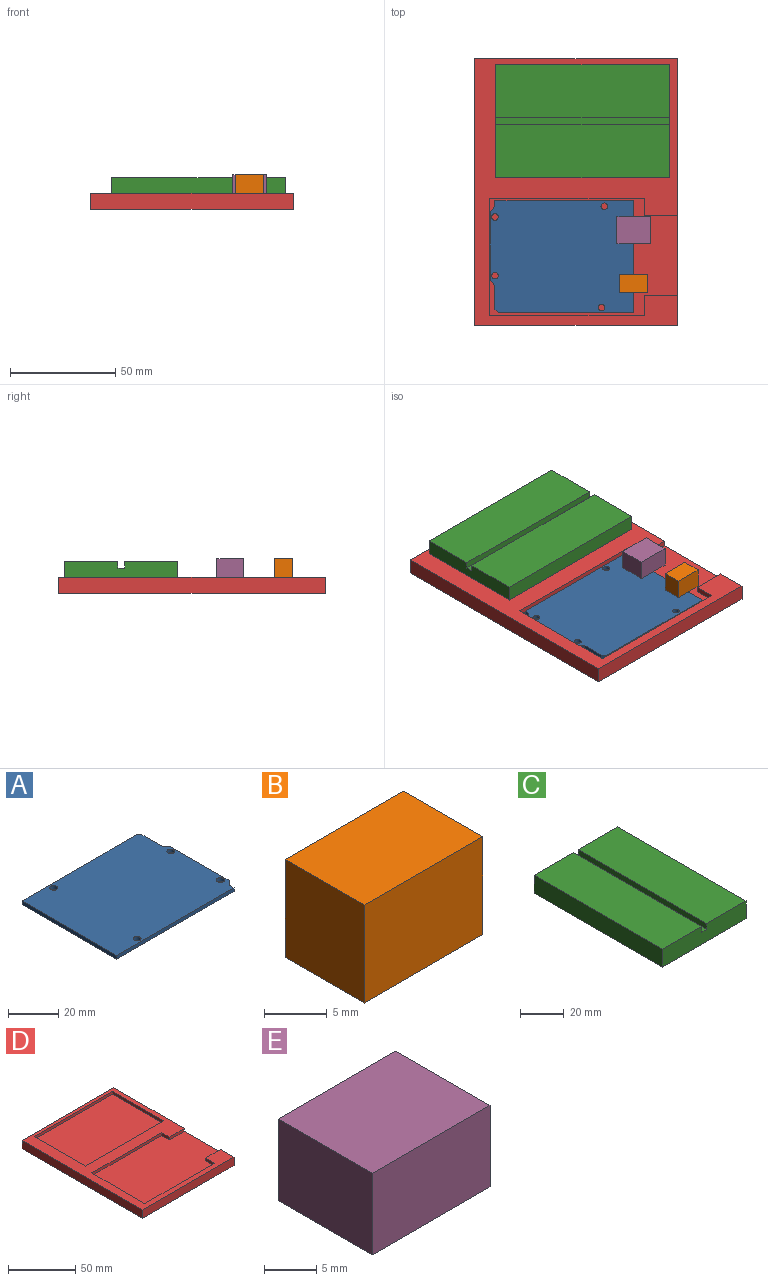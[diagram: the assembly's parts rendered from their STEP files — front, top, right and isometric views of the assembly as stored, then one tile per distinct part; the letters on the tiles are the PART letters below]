
ASSEMBLY  parts=5 mates=4
PART A: 15 faces, bbox 68.3x53.3x1.8 mm
  f0: plane 66.04x1.78mm, normal (0,-1,0), area 117.4mm2, adj f1,f11,f13,f14
  f1: plane 2.54x1.78mm, normal (1,0,0), area 4.5mm2, adj f0,f2,f13,f14
  f2: plane 2.54x2.27mm, normal (0.75,-0.67,0), area 6.1mm2, adj f1,f3,f13,f14
  f3: plane 32.77x1.78mm, normal (1,0,0), area 58.3mm2, adj f2,f4,f13,f14
  f4: plane 2.54x2.27mm, normal (0.75,0.67,0), area 6.1mm2, adj f3,f5,f13,f14
  f5: plane 11.43x1.78mm, normal (1,0,0), area 20.3mm2, adj f4,f6,f13,f14
  f6: plane 1.78x1.52mm, normal (0.71,0.71,0), area 3.8mm2, adj f5,f7,f13,f14
  f7: plane 64.52x1.78mm, normal (0,1,0), area 114.7mm2, adj f6,f11,f13,f14
  f8: cylinder r=1.59mm len=3.18mm, axis (0,0,-1), area 17.7mm2, adj f13,f14
  f9: cylinder r=1.59mm len=3.18mm, axis (0,0,-1), area 17.7mm2, adj f13,f14
  f10: cylinder r=1.59mm len=3.18mm, axis (0,0,-1), area 17.7mm2, adj f13,f14
  f11: plane 53.34x1.78mm, normal (-1,0,0), area 94.8mm2, adj f0,f7,f13,f14
  f12: cylinder r=1.59mm len=3.18mm, axis (0,0,-1), area 17.7mm2, adj f13,f14
  f13: plane 68.31x53.34mm, normal (0,0,1), area 3569.8mm2, adj f0,f1,f2,f3,f4,f5,f6,f7
  f14: plane 68.31x53.34mm, normal (0,0,-1), area 3569.8mm2, adj f0,f1,f2,f3,f4,f5,f6,f7
PART B: 6 faces, bbox 13.3x8.9x9.5 mm
  f0: plane 13.34x9.53mm, normal (0,-1,0), area 127mm2, adj f1,f3,f4,f5
  f1: plane 9.53x8.89mm, normal (1,0,0), area 84.7mm2, adj f0,f2,f4,f5
  f2: plane 13.34x9.53mm, normal (0,1,0), area 127mm2, adj f1,f3,f4,f5
  f3: plane 9.53x8.89mm, normal (-1,0,0), area 84.7mm2, adj f0,f2,f4,f5
  f4: plane 13.34x8.89mm, normal (0,0,1), area 118.5mm2, adj f0,f1,f2,f3
  f5: plane 13.34x8.89mm, normal (0,0,-1), area 118.5mm2, adj f0,f1,f2,f3
PART C: 10 faces, bbox 54x82.6x10 mm
  f0: plane 82.55x25.4mm, normal (0,0,1), area 2096.8mm2, adj f1,f3,f4,f7
  f1: plane 53.98x10mm, normal (0,1,0), area 529.7mm2, adj f0,f2,f4,f5,f6,f7,f8,f9
  f2: plane 82.55x10mm, normal (-1,0,0), area 825.5mm2, adj f1,f3,f5,f6
  f3: plane 53.98x10mm, normal (0,-1,0), area 529.7mm2, adj f0,f2,f4,f5,f6,f7,f8,f9
  f4: plane 82.55x10mm, normal (1,0,0), area 825.5mm2, adj f0,f1,f3,f6
  f5: plane 82.55x25.4mm, normal (0,0,1), area 2096.8mm2, adj f1,f2,f3,f8
  f6: plane 82.55x53.98mm, normal (0,0,-1), area 4455.6mm2, adj f1,f2,f3,f4
  f7: plane 82.55x3.18mm, normal (-1,0,0), area 262.1mm2, adj f0,f1,f3,f9
  f8: plane 82.55x3.18mm, normal (1,0,0), area 262.1mm2, adj f1,f3,f5,f9
  f9: plane 82.55x3.18mm, normal (0,0,1), area 262.1mm2, adj f1,f3,f7,f8
PART D: 19 faces, bbox 96.5x127x7.6 mm
  f0: plane 127x96.52mm, normal (0,0,1), area 3085.7mm2, adj f1,f2,f3,f4,f5,f7,f8,f9
  f1: plane 127x7.62mm, normal (1,0,0), area 871mm2, adj f0,f3,f5,f6,f11,f17,f18
  f2: plane 8.21x2.54mm, normal (-1,0,0), area 20.8mm2, adj f0,f7,f11,f17
  f3: plane 96.52x7.62mm, normal (0,1,0), area 735.5mm2, adj f0,f1,f4,f6
  f4: plane 127x7.62mm, normal (-1,0,0), area 967.7mm2, adj f0,f3,f5,f6
  f5: plane 96.52x7.62mm, normal (0,-1,0), area 735.5mm2, adj f0,f1,f4,f6
  f6: plane 127x96.52mm, normal (0,0,-1), area 12258mm2, adj f1,f3,f4,f5
  f7: plane 73.66x2.54mm, normal (0,-1,0), area 187.1mm2, adj f0,f2,f8,f11
  f8: plane 55.88x2.54mm, normal (1,0,0), area 141.9mm2, adj f0,f7,f9,f11
  f9: plane 73.66x2.54mm, normal (0,1,0), area 187.1mm2, adj f0,f8,f10,f11
  f10: plane 9.57x2.54mm, normal (-1,0,0), area 24.3mm2, adj f0,f9,f11,f18
  f11: plane 89.42x55.88mm, normal (0,0,1), area 4716.7mm2, adj f1,f2,f7,f8,f9,f10,f17,f18
  f12: plane 53.98x2.54mm, normal (1,0,0), area 137.1mm2, adj f0,f13,f15,f16
  f13: plane 82.55x2.54mm, normal (0,1,0), area 209.7mm2, adj f0,f12,f14,f16
  f14: plane 53.98x2.54mm, normal (-1,0,0), area 137.1mm2, adj f0,f13,f15,f16
  f15: plane 82.55x2.54mm, normal (0,-1,0), area 209.7mm2, adj f0,f12,f14,f16
  f16: plane 82.55x53.98mm, normal (0,0,1), area 4455.6mm2, adj f12,f13,f14,f15
  f17: plane 15.76x2.54mm, normal (0,-1,0), area 40mm2, adj f0,f1,f2,f11
  f18: plane 15.76x2.54mm, normal (0,1,0), area 40mm2, adj f0,f1,f10,f11
PART E: 6 faces, bbox 15.9x12.7x9.5 mm
  f0: plane 15.88x9.53mm, normal (0,-1,0), area 151.2mm2, adj f1,f3,f4,f5
  f1: plane 12.7x9.53mm, normal (1,0,0), area 121mm2, adj f0,f2,f4,f5
  f2: plane 15.88x9.53mm, normal (0,1,0), area 151.2mm2, adj f1,f3,f4,f5
  f3: plane 12.7x9.53mm, normal (-1,0,0), area 121mm2, adj f0,f2,f4,f5
  f4: plane 15.88x12.7mm, normal (0,0,1), area 201.6mm2, adj f0,f1,f2,f3
  f5: plane 15.88x12.7mm, normal (0,0,-1), area 201.6mm2, adj f0,f1,f2,f3
PLACE A rot(axis=(0,0,1),180deg) t=(-33.74,-7.41,34.18)mm
PLACE B t=(-38.51,-54.4,34.18)mm
PLACE C rot(axis=(0,0,-1),90deg) t=(-50.09,25.48,34.18)mm
PLACE D t=(-54.85,-3.7,29.1)mm
PLACE E t=(-35.33,-60.12,34.18)mm
MATE fastened C.f6 <-> D.f16  axis (0,0,-1) through (-58.1,30.5,34.18)mm
MATE fastened A.f14 <-> D.f11  axis (0,0,-1) through (-67.45,-33.98,34.18)mm
MATE fastened B.f5 <-> A.f13  axis (0,0,-1) through (-33.74,-46.78,35.95)mm
MATE fastened E.f5 <-> A.f13  axis (0,0,-1) through (-33.74,-21.38,35.95)mm
